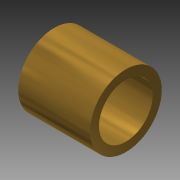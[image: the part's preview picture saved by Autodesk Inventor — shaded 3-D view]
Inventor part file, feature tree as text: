
AUTODESK INVENTOR PART (.ipt)
format: ipt  version: 2014 SP1 (Build 180222100, 222)  size: 99,840 bytes
history: native  units: mm
features: extrude x1, sketch x1
ambient origin geometry x8: Origin, YZ Plane, XZ Plane, XY Plane, X Axis, Y Axis, Z Axis, Center Point
bodies: Solid1 (feature_tree)
feature tree (2):
  extrude  "Extrusion1"  Depth=12.7mm
  sketch  "Sketch1"  dims[d0=9.525mm d1=12.7mm d2=12.7mm d3=0.0mm]
